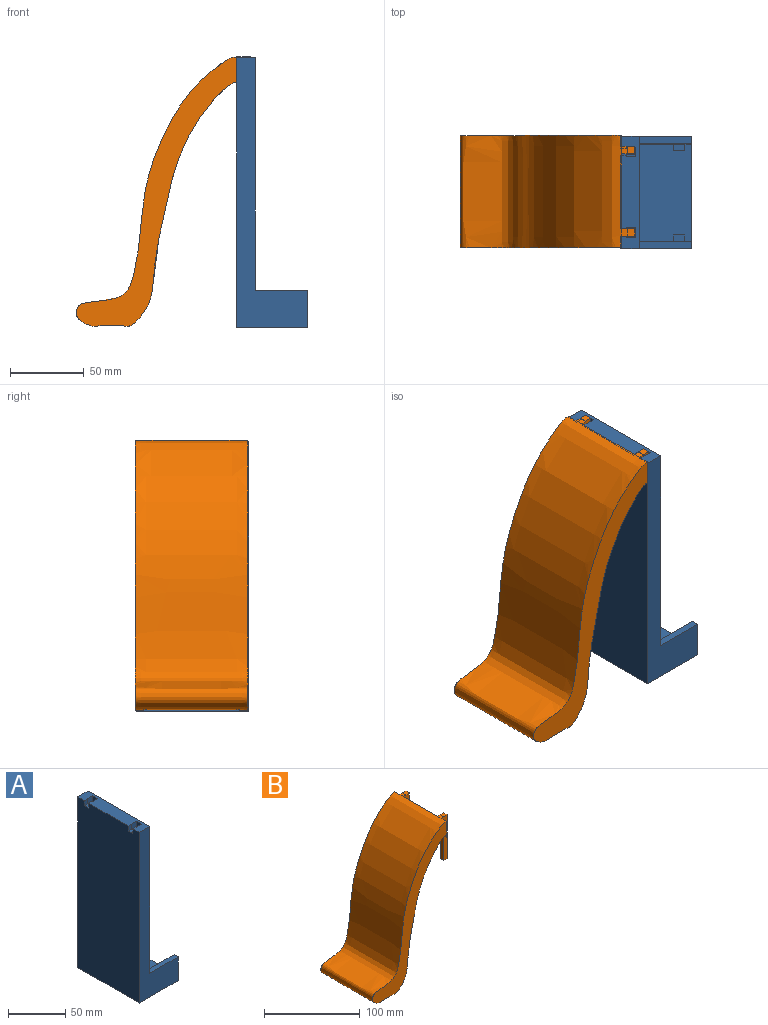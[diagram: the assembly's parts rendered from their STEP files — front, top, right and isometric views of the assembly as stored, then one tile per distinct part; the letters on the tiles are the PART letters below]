
ASSEMBLY  parts=2 mates=1
PART A: 36 faces, bbox 48.3x76.2x183.2 mm
  f0: plane 66.11x35.56mm, normal (0,0,1), area 2284.2mm2, adj f1,f2,f9,f11,f12,f13,f14,f16
  f1: plane 35.56x20.32mm, normal (0,-1,0), area 672.3mm2, adj f0,f2,f8,f9,f12,f13,f15
  f2: plane 178.15x76.2mm, normal (1,0,0), area 13369.8mm2, adj f0,f1,f3,f6,f7,f8,f10,f11
  f3: plane 76.2x12.7mm, normal (0,0,1), area 846.4mm2, adj f2,f4,f6,f7,f20,f21,f22,f23
  f4: plane 183.23x76.2mm, normal (-1,0,0), area 13904.9mm2, adj f3,f5,f6,f7,f30,f31,f32,f33
  f5: plane 76.2x48.26mm, normal (0,0,-1), area 3677.4mm2, adj f4,f6,f7,f9
  f6: plane 183.23x48.26mm, normal (0,-1,0), area 3230.2mm2, adj f2,f3,f4,f5,f9,f10
  f7: plane 183.23x48.26mm, normal (0,1,0), area 3230.2mm2, adj f2,f3,f4,f5,f8,f9
  f8: plane 35.56x5.07mm, normal (0,0,1), area 180.2mm2, adj f1,f2,f7,f9
  f9: plane 76.2x25.4mm, normal (1,0,0), area 592mm2, adj f0,f1,f5,f6,f7,f8,f10,f11
  f10: plane 35.56x5.02mm, normal (0,0,1), area 178.5mm2, adj f2,f6,f9,f11
  f11: plane 35.56x20.32mm, normal (0,1,0), area 672.3mm2, adj f0,f2,f9,f10,f16,f18,f19
  f12: plane 6.6x4.38mm, normal (1,0,0), area 28.9mm2, adj f0,f1,f14,f15
  f13: plane 6.6x4.38mm, normal (-1,0,0), area 28.9mm2, adj f0,f1,f14,f15
  f14: plane 7.62x6.6mm, normal (0,-1,0), area 50.3mm2, adj f0,f12,f13,f15
  f15: plane 7.62x4.38mm, normal (0,0,1), area 33.4mm2, adj f1,f12,f13,f14
  f16: plane 6.6x4.38mm, normal (1,0,0), area 28.9mm2, adj f0,f11,f17,f19
  f17: plane 7.62x6.6mm, normal (0,1,0), area 50.3mm2, adj f0,f16,f18,f19
  f18: plane 6.6x4.38mm, normal (-1,0,0), area 28.9mm2, adj f0,f11,f17,f19
  f19: plane 7.62x4.38mm, normal (0,0,1), area 33.4mm2, adj f11,f16,f17,f18
  f20: plane 55.88x6.35mm, normal (1,0,0), area 326.4mm2, adj f3,f21,f23,f24,f33,f34,f35
  f21: plane 55.88x6.35mm, normal (0,1,0), area 354.8mm2, adj f3,f20,f22,f24
  f22: plane 55.88x6.35mm, normal (-1,0,0), area 354.8mm2, adj f3,f21,f23,f24
  f23: plane 55.88x6.35mm, normal (0,-1,0), area 354.8mm2, adj f3,f20,f22,f24
  f24: plane 6.35x6.35mm, normal (0,0,1), area 40.3mm2, adj f20,f21,f22,f23
  f25: plane 55.88x6.35mm, normal (1,0,0), area 326.4mm2, adj f3,f26,f28,f29,f30,f31,f32
  f26: plane 55.88x6.35mm, normal (0,1,0), area 354.8mm2, adj f3,f25,f27,f29
  f27: plane 55.88x6.35mm, normal (-1,0,0), area 354.8mm2, adj f3,f26,f28,f29
  f28: plane 55.88x6.35mm, normal (0,-1,0), area 354.8mm2, adj f3,f25,f27,f29
  f29: plane 6.35x6.35mm, normal (0,0,1), area 40.3mm2, adj f25,f26,f27,f28
  f30: plane 5.33x3.81mm, normal (0,-1,0), area 20.3mm2, adj f3,f4,f25,f32
  f31: plane 5.33x3.81mm, normal (0,1,0), area 20.3mm2, adj f3,f4,f25,f32
  f32: plane 5.33x3.81mm, normal (0,0,1), area 20.3mm2, adj f4,f25,f30,f31
  f33: plane 5.33x3.81mm, normal (0,-1,0), area 20.3mm2, adj f3,f4,f20,f35
  f34: plane 5.33x3.81mm, normal (0,1,0), area 20.3mm2, adj f3,f4,f20,f35
  f35: plane 5.33x3.81mm, normal (0,0,1), area 20.3mm2, adj f4,f20,f33,f34
PART B: 22 faces, bbox 119.4x76.2x184.4 mm
  f0: plane 50.53x5.08mm, normal (-1,0,0), area 256.7mm2, adj f6,f7,f8,f20
  f1: plane 55.88x5.08mm, normal (1,0,0), area 283.9mm2, adj f6,f8,f15,f20
  f2: plane 76.2x20.27mm, normal (1,0,0), area 1492.9mm2, adj f3,f4,f5,f6,f7,f8,f10,f11
  f3: extruded ~182.94x109.23mm, area 34855.1mm2, adj f2,f4,f5,f9,f13
  f4: plane 184.16x110.51mm, normal (0,-1,0), area 3419.9mm2, adj f2,f3
  f5: plane 184.16x110.51mm, normal (0,1,0), area 3419.9mm2, adj f2,f3
  f6: plane 55.88x8.89mm, normal (0,-1,0), area 303.2mm2, adj f0,f1,f2,f7,f9,f14,f15,f20
  f7: plane 5.08x3.81mm, normal (0,0,-1), area 19.4mm2, adj f0,f2,f6,f8
  f8: plane 55.88x8.89mm, normal (0,1,0), area 303.2mm2, adj f0,f1,f2,f7,f9,f14,f15,f20
  f9: plane 5.08x3.81mm, normal (0,0,1), area 19.4mm2, adj f3,f6,f8,f14
  f10: plane 55.88x8.89mm, normal (0,-1,0), area 303.2mm2, adj f2,f11,f13,f16,f17,f18,f19,f21
  f11: plane 5.08x3.81mm, normal (0,0,-1), area 19.4mm2, adj f2,f10,f12,f16
  f12: plane 55.88x8.89mm, normal (0,1,0), area 303.2mm2, adj f2,f11,f13,f16,f17,f18,f19,f21
  f13: plane 5.08x3.81mm, normal (0,0,1), area 19.4mm2, adj f3,f10,f12,f17
  f14: plane 5.08x0.27mm, normal (-1,0,0), area 1.3mm2, adj f6,f8,f9,f15
  f15: plane 5.08x5.08mm, normal (0,0,1), area 25.8mm2, adj f1,f6,f8,f14
  f16: plane 50.54x5.08mm, normal (-1,0,0), area 256.7mm2, adj f10,f11,f12,f21
  f17: plane 5.08x0.27mm, normal (-1,0,0), area 1.3mm2, adj f10,f12,f13,f19
  f18: plane 55.88x5.08mm, normal (1,0,0), area 283.9mm2, adj f10,f12,f19,f21
  f19: plane 5.08x5.08mm, normal (0,0,1), area 25.8mm2, adj f10,f12,f17,f18
  f20: plane 5.08x5.08mm, normal (0,0,-1), area 25.8mm2, adj f0,f1,f6,f8
  f21: plane 5.08x5.08mm, normal (0,0,-1), area 25.8mm2, adj f10,f12,f16,f18
PLACE A t=(-92.32,141.38,-34.45)mm
PLACE B t=(-91.68,142.01,-33.6)mm
MATE slider B.f21 <-> A.f24  axis (0,0,-1) through (-85.33,75.97,93.75)mm
